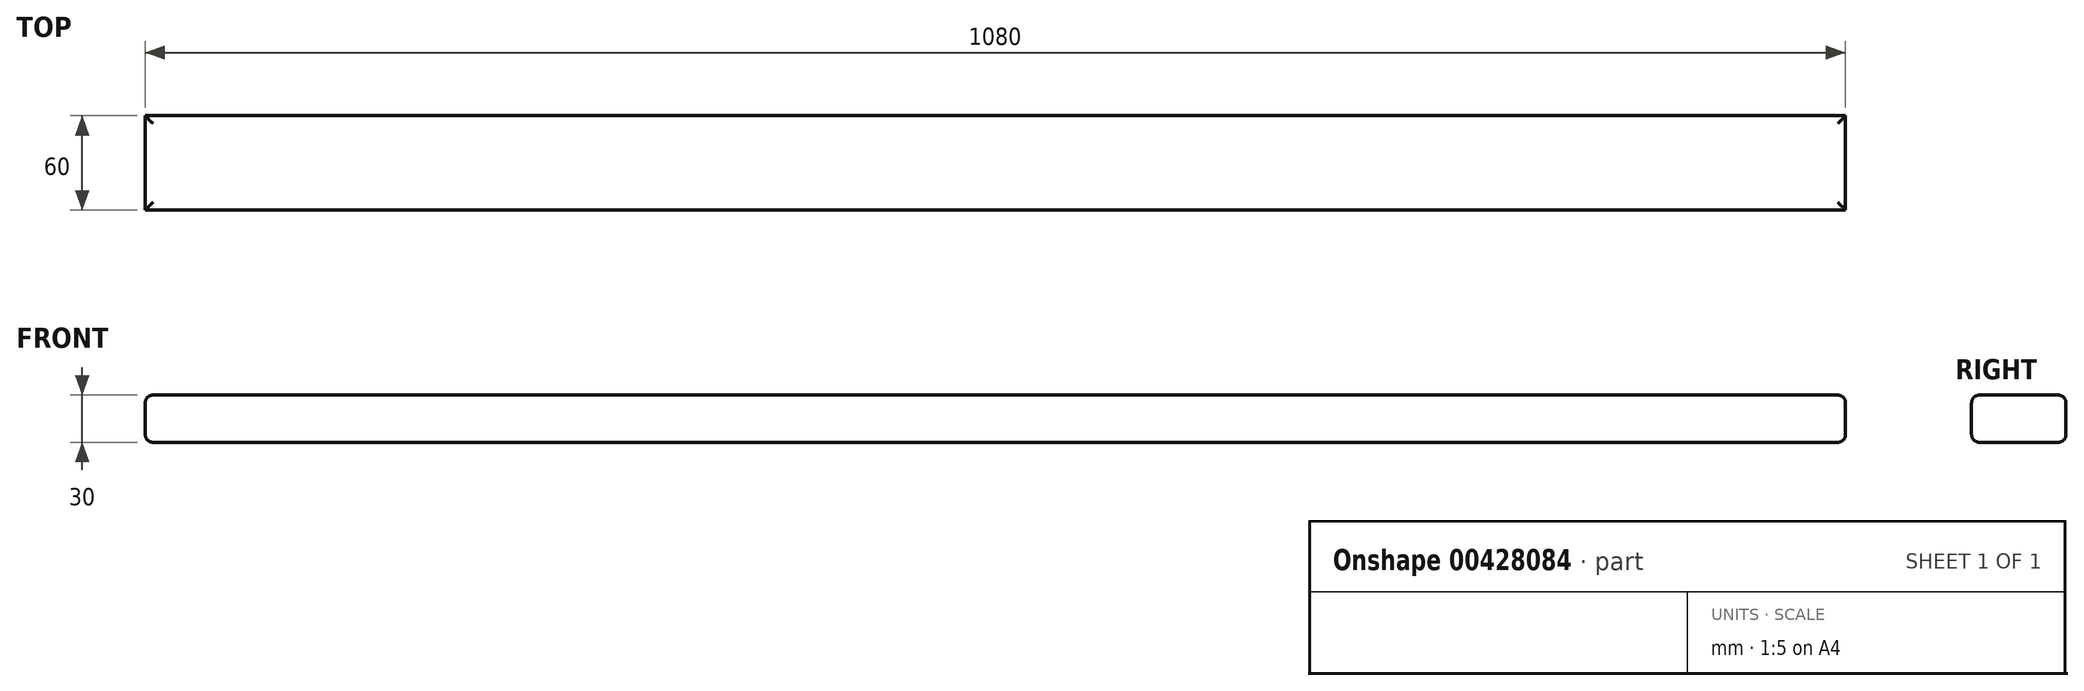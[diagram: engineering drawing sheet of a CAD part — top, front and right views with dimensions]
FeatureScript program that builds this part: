
annotation { "Feature Type Name" : "Feature", "Feature Type Description" : "" }
export const myFeature = defineFeature(function(context is Context, id is Id, definition is map)
    precondition{}
    {
        {
            var Q0;
            Q0=qCreatedBy(makeId("Top.planeOp"),FACE);
            var sketch = newSketch(context, id + "F0", { "sketchPlane" : qUnion([Q0])});
            skLineSegment(sketch, "E0.bottom", {"start": v(540, 30) * mm, "end": v(-540, 30) * mm});
            skLineSegment(sketch, "E0.top", {"start": v(540, -30) * mm, "end": v(-540, -30) * mm});
            skLineSegment(sketch, "E0.left", {"start": v(540, 30) * mm, "end": v(540, -30) * mm});
            skLineSegment(sketch, "E0.right", {"start": v(-540, 30) * mm, "end": v(-540, -30) * mm});
            skPoint(sketch, "E0.middle", {"position": v(0, 0) * mm});
            skSolve(sketch);
        }
        {
            var Q0;
            Q0=makeQuery(id+"F0.imprint","IMPRINT",FACE,{"disambiguationData":[TD([[makeQuery(id+"F0.imprint","IMPRINT",EDGE,{"derivedFrom":sQuery(id+"F0.wireOp",EDGE,"E0.bottom")}),1.0]])]});
            extrude(context, id + "F1", {"entities" : qUnion([Q0]), "depth" : 30 * mm});
        }
        {
            var Q0;
            Q0=makeQuery(id+"F1.opExtrude","CAP_FACE",FACE,{"disambiguationData":[OSD([sQuery(id+"F0.wireOp",EDGE,"E0.bottom"),sQuery(id+"F0.wireOp",EDGE,"E0.top"),sQuery(id+"F0.wireOp",EDGE,"E0.left"),sQuery(id+"F0.wireOp",EDGE,"E0.right")])],"isStart":false});
            var Q1;
            Q1=makeQuery(id+"F1.opExtrude","CAP_FACE",FACE,{"disambiguationData":[OSD([sQuery(id+"F0.wireOp",EDGE,"E0.bottom"),sQuery(id+"F0.wireOp",EDGE,"E0.top"),sQuery(id+"F0.wireOp",EDGE,"E0.left"),sQuery(id+"F0.wireOp",EDGE,"E0.right")])],"isStart":true});
            fillet(context, id + "F2", {"entities" : qUnion([Q0, Q1]), "radius" : 5 * mm, "tangentPropagation" : true, "allowEdgeOverflow" : false});
        }
    });
